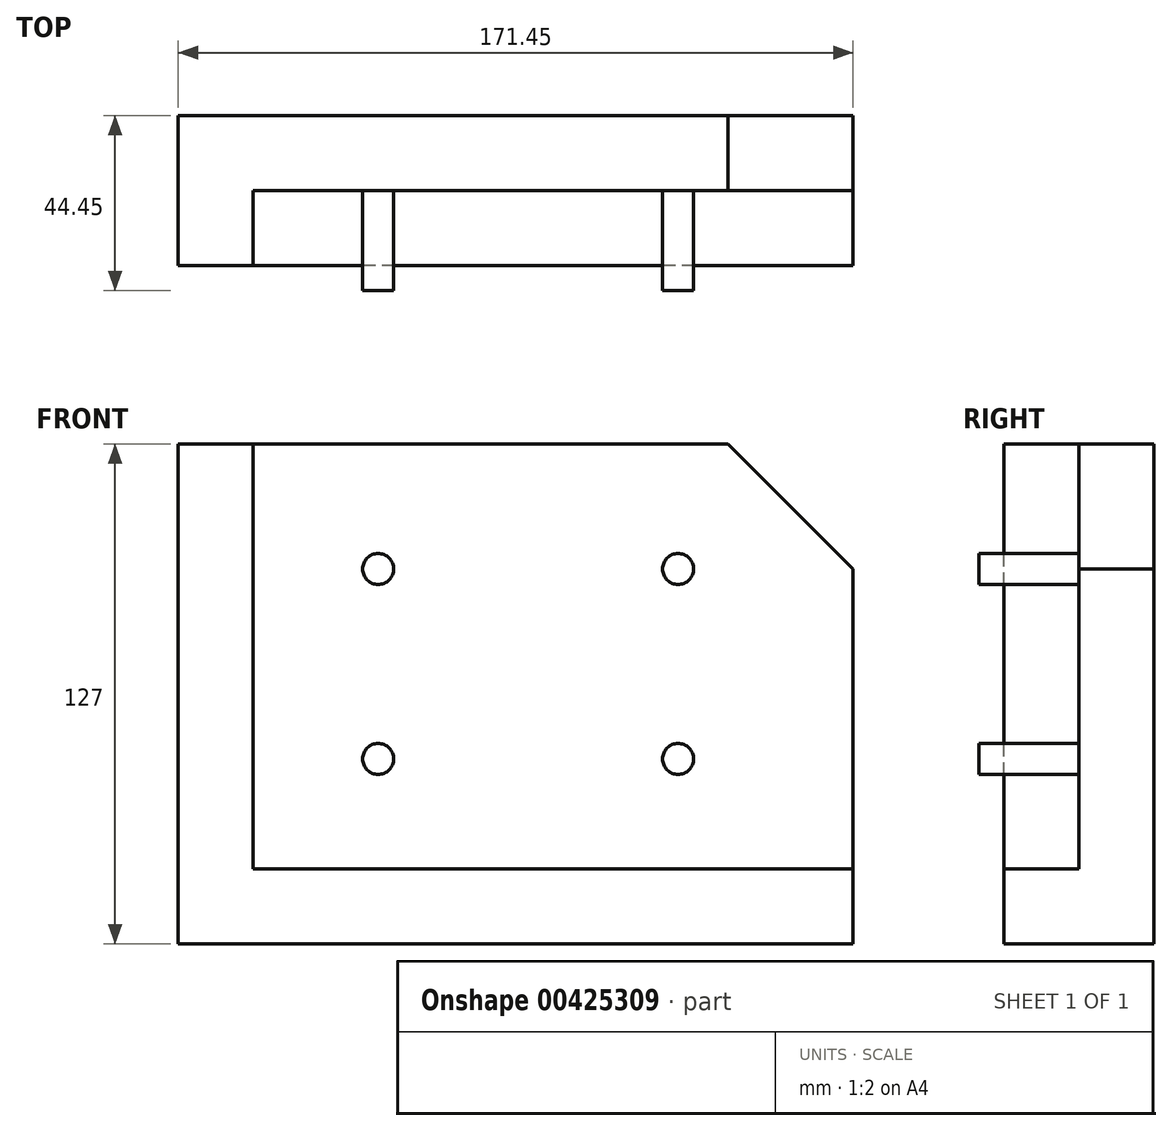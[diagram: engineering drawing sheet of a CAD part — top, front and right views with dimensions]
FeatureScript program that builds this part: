
annotation { "Feature Type Name" : "Feature", "Feature Type Description" : "" }
export const myFeature = defineFeature(function(context is Context, id is Id, definition is map)
    precondition{}
    {
        {
            var Q0;
            Q0=qCreatedBy(makeId("Front.planeOp"),FACE);
            var sketch = newSketch(context, id + "F0", { "sketchPlane" : qUnion([Q0])});
            skLineSegment(sketch, "E0", {"start": v(9.3, 0) * mm, "end": v(171.45, 0) * mm});
            skLineSegment(sketch, "E1", {"start": v(171.45, 0) * mm, "end": v(171.45, 19.05) * mm});
            skLineSegment(sketch, "E2", {"start": v(171.45, 19.05) * mm, "end": v(19.05, 19.05) * mm});
            skLineSegment(sketch, "E3", {"start": v(19.05, 19.05) * mm, "end": v(19.05, 127) * mm});
            skLineSegment(sketch, "E4", {"start": v(19.05, 127) * mm, "end": v(0, 127) * mm});
            skLineSegment(sketch, "E5", {"start": v(0, 127) * mm, "end": v(0, 0) * mm});
            skLineSegment(sketch, "E6", {"start": v(0, 0) * mm, "end": v(9.3, 0) * mm});
            skSolve(sketch);
        }
        {
            var Q0;
            Q0 = qSketchRegion(id + "F0", true);
            extrude(context, id + "F1", {"entities" : qUnion([Q0]), "depth" : 38.1 * mm});
        }
        {
            var Q0;
            Q0=makeQuery(id+"F1.opExtrude","SWEPT_FACE",FACE,{"disambiguationData":[OSD([sQuery(id+"F0.wireOp",EDGE,"E3")])]});
            var sketch = newSketch(context, id + "F2", { "sketchPlane" : qUnion([Q0])});
            skLineSegment(sketch, "E7.bottom", {"start": v(0, 127) * mm, "end": v(-19.05, 127) * mm});
            skLineSegment(sketch, "E7.top", {"start": v(0, 19.05) * mm, "end": v(-19.05, 19.05) * mm});
            skLineSegment(sketch, "E7.left", {"start": v(0, 127) * mm, "end": v(0, 19.05) * mm});
            skLineSegment(sketch, "E7.right", {"start": v(-19.05, 127) * mm, "end": v(-19.05, 19.05) * mm});
            skSolve(sketch);
        }
        {
            var Q0;
            Q0 = qSketchRegion(id + "F2", true);
            var Q1;
            Q1=makeQuery(id+"F1.opExtrude","SWEPT_FACE",FACE,{"disambiguationData":[OSD([sQuery(id+"F0.wireOp",EDGE,"E1")])]});
            extrude(context, id + "F3", {"entities" : qUnion([Q0]), "operationType" : NewBodyOperationType.ADD, "endBound" : BoundingType.UP_TO_SURFACE, "endBoundEntityFace" : qUnion([Q1]), "depth" : 25.4 * mm});
        }
        {
            var Q0;
            Q0=makeQuery(id+"F3.opExtrude","CAP_EDGE",EDGE,{"disambiguationData":[OSD([sQuery(id+"F2.wireOp",EDGE,"E7.bottom")])],"isStart":false});
            chamfer(context, id + "F4", {"entities" : qUnion([Q0]), "width" : 31.75 * mm, "tangentPropagation" : true});
        }
        {
            var Q0;
            Q0=makeQuery(id+"F3.opExtrude","SWEPT_FACE",FACE,{"disambiguationData":[OSD([sQuery(id+"F2.wireOp",EDGE,"E7.right")])]});
            var sketch = newSketch(context, id + "F5", { "sketchPlane" : qUnion([Q0])});
            skLineSegment(sketch, "E8.bottom", {"start": v(50.8, 95.25) * mm, "end": v(127, 95.25) * mm, "construction": true});
            skLineSegment(sketch, "E8.top", {"start": v(50.8, 47) * mm, "end": v(127, 47) * mm, "construction": true});
            skLineSegment(sketch, "E8.left", {"start": v(50.8, 95.25) * mm, "end": v(50.8, 47) * mm, "construction": true});
            skLineSegment(sketch, "E8.right", {"start": v(127, 95.25) * mm, "end": v(127, 47) * mm, "construction": true});
            skCircle(sketch, "E9", {"center": v(50.8, 95.25) * mm, "radius": 3.94 * mm});
            skCircle(sketch, "E10", {"center": v(127, 95.25) * mm, "radius": 3.94 * mm});
            skCircle(sketch, "E11", {"center": v(127, 47) * mm, "radius": 3.94 * mm});
            skCircle(sketch, "E12", {"center": v(50.8, 47) * mm, "radius": 3.94 * mm});
            skSolve(sketch);
        }
        {
            var Q0;
            Q0 = qSketchRegion(id + "F5", true);
            extrude(context, id + "F6", {"entities" : qUnion([Q0]), "operationType" : NewBodyOperationType.ADD, "depth" : 25.4 * mm});
        }
    });
